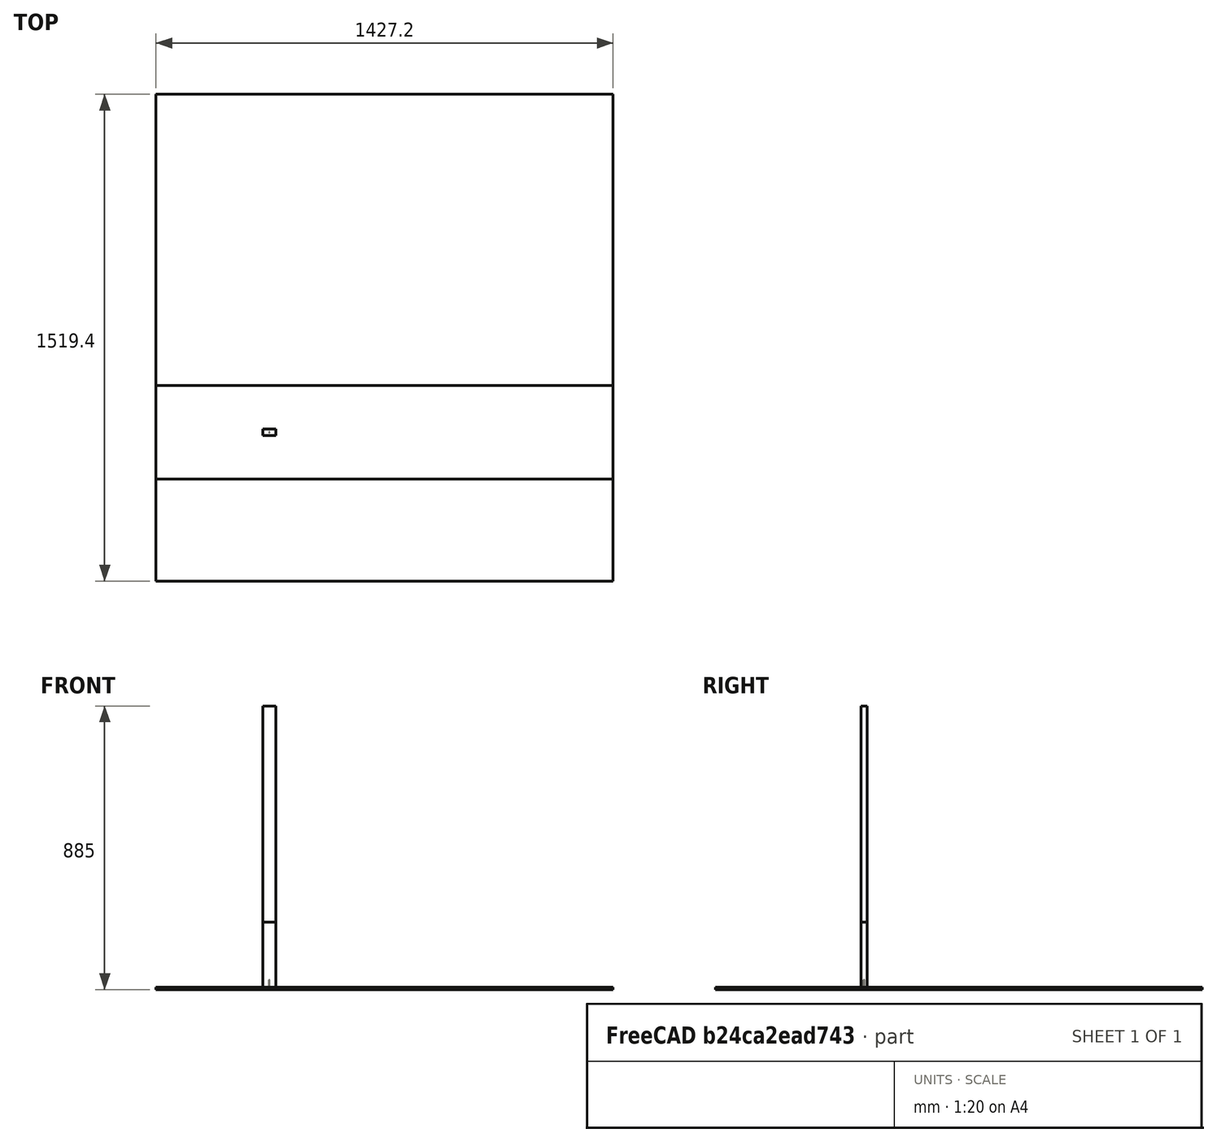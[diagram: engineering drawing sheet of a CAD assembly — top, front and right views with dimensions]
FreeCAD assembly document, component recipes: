
FREECAD ASSEMBLY — COMPONENT RECIPES ("composit_stand10_transport")

This assembly document has 12 components, labeled P0..P11 below (a component is one placed body or linked part). 12 of them carry a construction recipe — the FreeCAD feature program that regenerates the part from scratch, quoted from this document or its linked companion documents; the rest are supplied as boundary geometry only. No exploded tour is included for this assembly.
COMPONENT P0 — recipe-attached ("bar_big001", modeled in this document).
Construction recipe (the document's own serialized feature program — sketch geometry with constraints, then the solid features built on it; lengths are millimeters unless a unit is written):

FEATURE [Sketcher::SketchObject] Sketch003  label="bar_big_Sketch"
  AttachmentSupport = -> [XY_Plane003]
  FullyConstrained = true
  MapMode = 5
  sketch-geometry (5):
    g0: LineSegment StartX=-20 StartY=-10 StartZ=0 EndX=20 EndY=-10 EndZ=0
    g1: LineSegment StartX=20 StartY=-10 StartZ=0 EndX=20 EndY=10 EndZ=0
    g2: LineSegment StartX=20 StartY=10 StartZ=0 EndX=-20 EndY=10 EndZ=0
    g3: LineSegment StartX=-20 StartY=10 StartZ=0 EndX=-20 EndY=-10 EndZ=0
    g4: GeomPoint X=0 Y=0 Z=0
  constraints (12):
    c: Coincident(g0,g1)
    c: Coincident(g1,g2)
    c: Coincident(g2,g3)
    c: Coincident(g3,g0)
    c: Horizontal(g0)
    c: Horizontal(g2)
    c: Vertical(g1)
    c: Vertical(g3)
    c: Symmetric(g2,g0,g4)
    c: Coincident(g4,g-1)
    c: DistanceX(g0,g1) = 40
    c: DistanceY(g0,g1) = 20
FEATURE [PartDesign::Pad] Pad003
  Direction = (0,0,1)
  Length = 885
  Length2 = 10
  Profile = -> Sketch003
  ReferenceAxis = -> Sketch003 [N_Axis]
  Suppressed = false
  Type = 0
FEATURE [PartDesign::CoordinateSystem] Local_CS006  label="bar_big_LCS"
  AttacherType = Attacher::AttachEngine3D
  AttachmentOffset = pos=(-20,10,0) rot=(0,0,1;0rad)
  AttachmentSupport = -> [XY_Plane003]
  MapMode = 5
  Placement = pos=(-20,10,0) rot=(0,0,1;0rad)
FEATURE [PartDesign::Body] Body003  label="bar_big"
  Group = -> [Sketch003,Pad003,Local_CS006]
  Origin = -> Origin003
  Tip = -> Pad003
COMPONENT P1 — same part as P0; its construction recipe is shown at P0.
COMPONENT P2 — same part as P0; its construction recipe is shown at P0.
COMPONENT P3 — same part as P0; its construction recipe is shown at P0.
COMPONENT P4 — recipe-attached ("bar_small001", modeled in this document).
Construction recipe (the document's own serialized feature program — sketch geometry with constraints, then the solid features built on it; lengths are millimeters unless a unit is written):

FEATURE [Sketcher::SketchObject] Sketch004  label="bar_small_Sketch"
  AttachmentSupport = -> [XY_Plane004]
  FullyConstrained = true
  MapMode = 5
  sketch-geometry (5):
    g0: LineSegment StartX=-20 StartY=-10 StartZ=0 EndX=20 EndY=-10 EndZ=0
    g1: LineSegment StartX=20 StartY=-10 StartZ=0 EndX=20 EndY=10 EndZ=0
    g2: LineSegment StartX=20 StartY=10 StartZ=0 EndX=-20 EndY=10 EndZ=0
    g3: LineSegment StartX=-20 StartY=10 StartZ=0 EndX=-20 EndY=-10 EndZ=0
    g4: GeomPoint X=0 Y=0 Z=0
  constraints (12):
    c: Coincident(g0,g1)
    c: Coincident(g1,g2)
    c: Coincident(g2,g3)
    c: Coincident(g3,g0)
    c: Horizontal(g0)
    c: Horizontal(g2)
    c: Vertical(g1)
    c: Vertical(g3)
    c: Symmetric(g2,g0,g4)
    c: Coincident(g4,g-1)
    c: DistanceX(g0,g1) = 40
    c: DistanceY(g0,g1) = 20
FEATURE [PartDesign::Pad] Pad004
  Direction = (0,0,1)
  Length = 210
  Length2 = 10
  Profile = -> Sketch004
  ReferenceAxis = -> Sketch004 [N_Axis]
  Suppressed = false
  Type = 0
FEATURE [PartDesign::CoordinateSystem] Local_CS012
  AttacherType = Attacher::AttachEngine3D
  AttachmentOffset = pos=(-20,105,-10) rot=(0.707107,-0.707107,0;3.14159rad)
  AttachmentSupport = -> [XZ_Plane004]
  MapMode = 5
  Placement = pos=(-20,10,105) rot=(0.57735,-0.57735,-0.57735;4.18879rad)
FEATURE [PartDesign::Body] Body004  label="bar_small"
  Group = -> [Sketch004,Pad004,Local_CS012]
  Origin = -> Origin004
  Tip = -> Pad004
COMPONENT P5 — same part as P4; its construction recipe is shown at P4.
COMPONENT P6 — recipe-attached ("bottom001 🔒", modeled in this document).
Construction recipe (the document's own serialized feature program — sketch geometry with constraints, then the solid features built on it; lengths are millimeters unless a unit is written):

FEATURE [Sketcher::SketchObject] Sketch001  label="bottom_Sketch"
  AttachmentSupport = -> [XY_Plane001]
  FullyConstrained = true
  MapMode = 5
  sketch-geometry (5):
    g0: LineSegment StartX=-355.5 StartY=-145 StartZ=0 EndX=355.5 EndY=-145 EndZ=0
    g1: LineSegment StartX=355.5 StartY=-145 StartZ=0 EndX=355.5 EndY=145 EndZ=0
    g2: LineSegment StartX=355.5 StartY=145 StartZ=0 EndX=-355.5 EndY=145 EndZ=0
    g3: LineSegment StartX=-355.5 StartY=145 StartZ=0 EndX=-355.5 EndY=-145 EndZ=0
    g4: GeomPoint X=0 Y=0 Z=0
  constraints (12):
    c: Coincident(g0,g1)
    c: Coincident(g1,g2)
    c: Coincident(g2,g3)
    c: Coincident(g3,g0)
    c: Horizontal(g0)
    c: Horizontal(g2)
    c: Vertical(g1)
    c: Vertical(g3)
    c: Symmetric(g2,g0,g4)
    c: Coincident(g4,g-1)
    c: DistanceX(g0,g1) = 711  'width'
    c: DistanceY(g0,g1) = 290  'length'
FEATURE [PartDesign::Pad] Pad001
  Direction = (0,0,1)
  Length = 6
  Length2 = 10
  Profile = -> Sketch001
  ReferenceAxis = -> Sketch001 [N_Axis]
  Suppressed = false
  Type = 0
FEATURE [PartDesign::CoordinateSystem] Local_CS001  label="bottom_front_LCS"
  AttacherType = Attacher::AttachEngine3D
  AttachmentOffset = pos=(0,-145,0) rot=(1,0,0;1.5708rad)
  AttachmentSupport = -> [XY_Plane001]
  MapMode = 5
  Placement = pos=(0,-145,0) rot=(1,0,0;1.5708rad)
  expr: .AttachmentOffset.Base.y = -<<bottom_Sketch>>.Constraints.length / 2
FEATURE [PartDesign::CoordinateSystem] Local_CS002  label="bottom_side_LCS"
  AttacherType = Attacher::AttachEngine3D
  AttachmentOffset = pos=(329.5,0,6) rot=(0.57735,0.57735,0.57735;2.0944rad)
  AttachmentSupport = -> [XY_Plane001]
  MapMode = 5
  Placement = pos=(329.5,0,6) rot=(0.57735,0.57735,0.57735;2.0944rad)
  expr: .AttachmentOffset.Base.x = <<bottom_Sketch>>.Constraints.width / 2 - 26 mm
FEATURE [PartDesign::CoordinateSystem] Local_CS003  label="bottom_back_LCS"
  AttacherType = Attacher::AttachEngine3D
  AttachmentOffset = pos=(0,145,0) rot=(0,0.707107,0.707107;3.14159rad)
  AttachmentSupport = -> [XY_Plane001]
  MapMode = 5
  Placement = pos=(0,145,0) rot=(0,0.707107,0.707107;3.14159rad)
  expr: .AttachmentOffset.Base.y = <<bottom_Sketch>>.Constraints.length / 2
FEATURE [PartDesign::CoordinateSystem] Local_CS004  label="bottom_side2_LCS"
  AttacherType = Attacher::AttachEngine3D
  AttachmentOffset = pos=(-329.5,0,6) rot=(0.57735,0.57735,0.57735;2.0944rad)
  AttachmentSupport = -> [XY_Plane001]
  MapMode = 5
  Placement = pos=(-329.5,0,6) rot=(0.57735,0.57735,0.57735;2.0944rad)
  expr: .AttachmentOffset.Base.x = -<<bottom_side_LCS>>.Placement.Base.x
FEATURE [PartDesign::CoordinateSystem] Local_CS007  label="bottom_bar_big1_LCS"
  AttacherType = Attacher::AttachEngine3D
  AttachmentOffset = pos=(355.5,145,6) rot=(0,0,1;-1.5708rad)
  AttachmentSupport = -> [XY_Plane001]
  MapMode = 5
  Placement = pos=(355.5,145,6) rot=(0,0,1;4.71239rad)
  expr: .AttachmentOffset.Base.x = <<bottom_Sketch>>.Constraints.width / 2
  expr: .AttachmentOffset.Base.y = <<bottom_Sketch>>.Constraints.length / 2
FEATURE [PartDesign::CoordinateSystem] Local_CS008  label="bottom_bar_big2_LCS"
  AttacherType = Attacher::AttachEngine3D
  AttachmentOffset = pos=(355.5,-105,6) rot=(0,0,1;-1.5708rad)
  AttachmentSupport = -> [XY_Plane001]
  MapMode = 5
  Placement = pos=(355.5,-105,6) rot=(0,0,1;4.71239rad)
  expr: .AttachmentOffset.Base.x = <<bottom_Sketch>>.Constraints.width / 2
  expr: .AttachmentOffset.Base.y = -<<bottom_Sketch>>.Constraints.length / 2 + 40 mm
FEATURE [PartDesign::CoordinateSystem] Local_CS009  label="bottom_bar_big3_LCS"
  AttacherType = Attacher::AttachEngine3D
  AttachmentOffset = pos=(-335.5,145,6) rot=(0,0,1;-1.5708rad)
  AttachmentSupport = -> [XY_Plane001]
  MapMode = 5
  Placement = pos=(-335.5,145,6) rot=(0,0,1;4.71239rad)
  expr: .AttachmentOffset.Base.x = -<<bottom_Sketch>>.Constraints.width / 2 + 20 mm
  expr: .AttachmentOffset.Base.y = <<bottom_Sketch>>.Constraints.length / 2
FEATURE [PartDesign::CoordinateSystem] Local_CS010  label="bottom_bar_big4_LCS"
  AttacherType = Attacher::AttachEngine3D
  AttachmentOffset = pos=(-355.5,-145,6) rot=(0,0,1;-1.5708rad)
  AttachmentSupport = -> [XY_Plane001]
  MapMode = 5
  Placement = pos=(-355.5,-145,6) rot=(0,0,1;4.71239rad)
  expr: .AttachmentOffset.Base.x = -<<bottom_Sketch>>.Constraints.width / 2
  expr: .AttachmentOffset.Base.y = -<<bottom_Sketch>>.Constraints.length / 2
FEATURE [Sketcher::SketchObject] Sketch006
  AttachmentSupport = -> [XY_Plane001]
  FullyConstrained = true
  MapMode = 5
  sketch-geometry (2):
    g0: Circle CenterX=325 CenterY=115 CenterZ=0 NormalX=0 NormalY=0 NormalZ=1 AngleXU=0 Radius=1.7
    g1: Circle CenterX=-325 CenterY=-115 CenterZ=0 NormalX=0 NormalY=0 NormalZ=1 AngleXU=0 Radius=1.7
  constraints (5):
    c: Symmetric(g0,g1,g-1)
    c: DistanceX(g0) = 325
    c: DistanceY(g0) = 115
    c: Equal(g0,g1)
    c: Diameter(g0) = 3.4
FEATURE [PartDesign::Pocket] Pocket001
  BaseFeature = -> Pad001
  Direction = (0,0,-1)
  Length = 5
  Length2 = 5
  Midplane = true
  Profile = -> Sketch006
  ReferenceAxis = -> Sketch006 [N_Axis]
  Suppressed = false
  Type = 1
FEATURE [PartDesign::Body] Body001  label="bottom"
  Group = -> [Sketch001,Pad001,Local_CS001,Local_CS002,Local_CS003,Local_CS004,Local_CS007,Local_CS008,Local_CS009,Local_CS010,Sketch006,Pocket001]
  Origin = -> Origin001
  Tip = -> Pocket001
COMPONENT P7 — same part as P6; its construction recipe is shown at P6.
COMPONENT P8 — recipe-attached ("front001", modeled in this document).
Construction recipe (the document's own serialized feature program — sketch geometry with constraints, then the solid features built on it; lengths are millimeters unless a unit is written):

FEATURE [Sketcher::SketchObject] Sketch  label="front_Sketch"
  AttachmentSupport = -> [XY_Plane]
  FullyConstrained = true
  MapMode = 5
  sketch-geometry (5):
    g0: LineSegment StartX=-355.5 StartY=-465.5 StartZ=0 EndX=355.5 EndY=-465.5 EndZ=0
    g1: LineSegment StartX=355.5 StartY=-465.5 StartZ=0 EndX=355.5 EndY=465.5 EndZ=0
    g2: LineSegment StartX=355.5 StartY=465.5 StartZ=0 EndX=-355.5 EndY=465.5 EndZ=0
    g3: LineSegment StartX=-355.5 StartY=465.5 StartZ=0 EndX=-355.5 EndY=-465.5 EndZ=0
    g4: GeomPoint X=0 Y=0 Z=0
  constraints (12):
    c: Coincident(g0,g1)
    c: Coincident(g1,g2)
    c: Coincident(g2,g3)
    c: Coincident(g3,g0)
    c: Horizontal(g0)
    c: Horizontal(g2)
    c: Vertical(g1)
    c: Vertical(g3)
    c: Symmetric(g2,g0,g4)
    c: Coincident(g4,g-1)
    c: DistanceX(g0,g1) = 711  'width'
    c: DistanceY(g0,g1) = 931  'height'
FEATURE [PartDesign::Pad] Pad
  Direction = (0,0,1)
  Length = 6
  Length2 = 10
  Profile = -> Sketch
  ReferenceAxis = -> Sketch [N_Axis]
  Suppressed = false
  Type = 0
FEATURE [PartDesign::CoordinateSystem] Local_CS  label="front_bottom_LCS"
  AttacherType = Attacher::AttachEngine3D
  AttachmentOffset = pos=(0,-445.5,0) rot=(0,0,1;0rad)
  AttachmentSupport = -> [XY_Plane]
  MapMode = 5
  Placement = pos=(0,-445.5,0) rot=(0,0,1;0rad)
  expr: .AttachmentOffset.Base.y = -<<front_Sketch>>.Constraints.height / 2 + 20 mm
FEATURE [Sketcher::SketchObject] Sketch005
  AttachmentSupport = -> [XY_Plane]
  FullyConstrained = true
  MapMode = 5
  sketch-geometry (2):
    g0: Circle CenterX=315 CenterY=430 CenterZ=0 NormalX=0 NormalY=0 NormalZ=1 AngleXU=0 Radius=1.7
    g1: Circle CenterX=-315 CenterY=-430 CenterZ=0 NormalX=0 NormalY=0 NormalZ=1 AngleXU=0 Radius=1.7
  constraints (5):
    c: Symmetric(g1,g0,g-1)
    c: Equal(g0,g1)
    c: Diameter(g0) = 3.4
    c: DistanceX(g0) = 315
    c: DistanceY(g0) = 430
FEATURE [PartDesign::Pocket] Pocket
  BaseFeature = -> Pad
  Direction = (0,0,-1)
  Length = 5
  Length2 = 5
  Midplane = true
  Profile = -> Sketch005
  ReferenceAxis = -> Sketch005 [N_Axis]
  Suppressed = false
  Type = 1
FEATURE [PartDesign::Body] Body  label="front"
  Group = -> [Sketch,Pad,Local_CS,Sketch005,Pocket]
  Origin = -> Origin
  Tip = -> Pocket
COMPONENT P9 — same part as P8; its construction recipe is shown at P8.
COMPONENT P10 — recipe-attached ("side001", modeled in this document).
Construction recipe (the document's own serialized feature program — sketch geometry with constraints, then the solid features built on it; lengths are millimeters unless a unit is written):

FEATURE [Sketcher::SketchObject] Sketch002  label="side_Sketch"
  AttachmentSupport = -> [XY_Plane002]
  FullyConstrained = true
  MapMode = 5
  sketch-geometry (5):
    g0: LineSegment StartX=-145 StartY=-442.5 StartZ=0 EndX=145 EndY=-442.5 EndZ=0
    g1: LineSegment StartX=145 StartY=-442.5 StartZ=0 EndX=145 EndY=442.5 EndZ=0
    g2: LineSegment StartX=145 StartY=442.5 StartZ=0 EndX=-145 EndY=442.5 EndZ=0
    g3: LineSegment StartX=-145 StartY=442.5 StartZ=0 EndX=-145 EndY=-442.5 EndZ=0
    g4: GeomPoint X=0 Y=0 Z=0
  constraints (12):
    c: Coincident(g0,g1)
    c: Coincident(g1,g2)
    c: Coincident(g2,g3)
    c: Coincident(g3,g0)
    c: Horizontal(g0)
    c: Horizontal(g2)
    c: Vertical(g1)
    c: Vertical(g3)
    c: Symmetric(g2,g0,g4)
    c: Coincident(g4,g-1)
    c: DistanceX(g0,g1) = 290  'length'
    c: DistanceY(g0,g1) = 885  'height'
FEATURE [PartDesign::Pad] Pad002
  Direction = (0,0,1)
  Length = 6
  Length2 = 10
  Profile = -> Sketch002
  ReferenceAxis = -> Sketch002 [N_Axis]
  Suppressed = false
  Type = 0
FEATURE [PartDesign::CoordinateSystem] Local_CS005  label="side_LCS"
  AttacherType = Attacher::AttachEngine3D
  AttachmentOffset = pos=(0,-442.5,0) rot=(0,0,1;0rad)
  AttachmentSupport = -> [XY_Plane002]
  MapMode = 5
  Placement = pos=(0,-442.5,0) rot=(0,0,1;0rad)
  expr: .AttachmentOffset.Base.y = -<<side_Sketch>>.Constraints.height / 2
FEATURE [PartDesign::CoordinateSystem] Local_CS011  label="side_bar_LCS"
  AttacherType = Attacher::AttachEngine3D
  AttachmentOffset = pos=(0,-442.5,6) rot=(0,0,1;0rad)
  AttachmentSupport = -> [XY_Plane002]
  MapMode = 5
  Placement = pos=(0,-442.5,6) rot=(0,0,1;0rad)
  expr: .AttachmentOffset.Base.y = -<<side_Sketch>>.Constraints.height / 2
FEATURE [Sketcher::SketchObject] Sketch007
  AttachmentSupport = -> [XY_Plane002]
  FullyConstrained = true
  MapMode = 5
  sketch-geometry (2):
    g0: Circle CenterX=130 CenterY=425 CenterZ=0 NormalX=0 NormalY=0 NormalZ=1 AngleXU=0 Radius=1.7
    g1: Circle CenterX=-130 CenterY=-425 CenterZ=0 NormalX=0 NormalY=0 NormalZ=1 AngleXU=0 Radius=1.7
  constraints (5):
    c: Symmetric(g0,g1,g-1)
    c: Equal(g0,g1)
    c: Diameter(g0) = 3.4
    c: DistanceX(g0) = 130
    c: DistanceY(g0) = 425
FEATURE [PartDesign::Pocket] Pocket002
  BaseFeature = -> Pad002
  Direction = (0,0,-1)
  Length = 5
  Length2 = 5
  Midplane = true
  Profile = -> Sketch007
  ReferenceAxis = -> Sketch007 [N_Axis]
  Suppressed = false
  Type = 1
FEATURE [PartDesign::Body] Body002  label="side"
  Group = -> [Sketch002,Pad002,Local_CS005,Local_CS011,Sketch007,Pocket002]
  Origin = -> Origin002
  Tip = -> Pocket002
COMPONENT P11 — same part as P10; its construction recipe is shown at P10.
PROVENANCE & LICENSES
A FreeCAD (.FCStd) document from a public repository crawl; recipes are the document's own serialized feature recipes (and, for linked parts, companion documents' recipes).
License: as declared in the source repository (recorded in the dataset sidecar).
